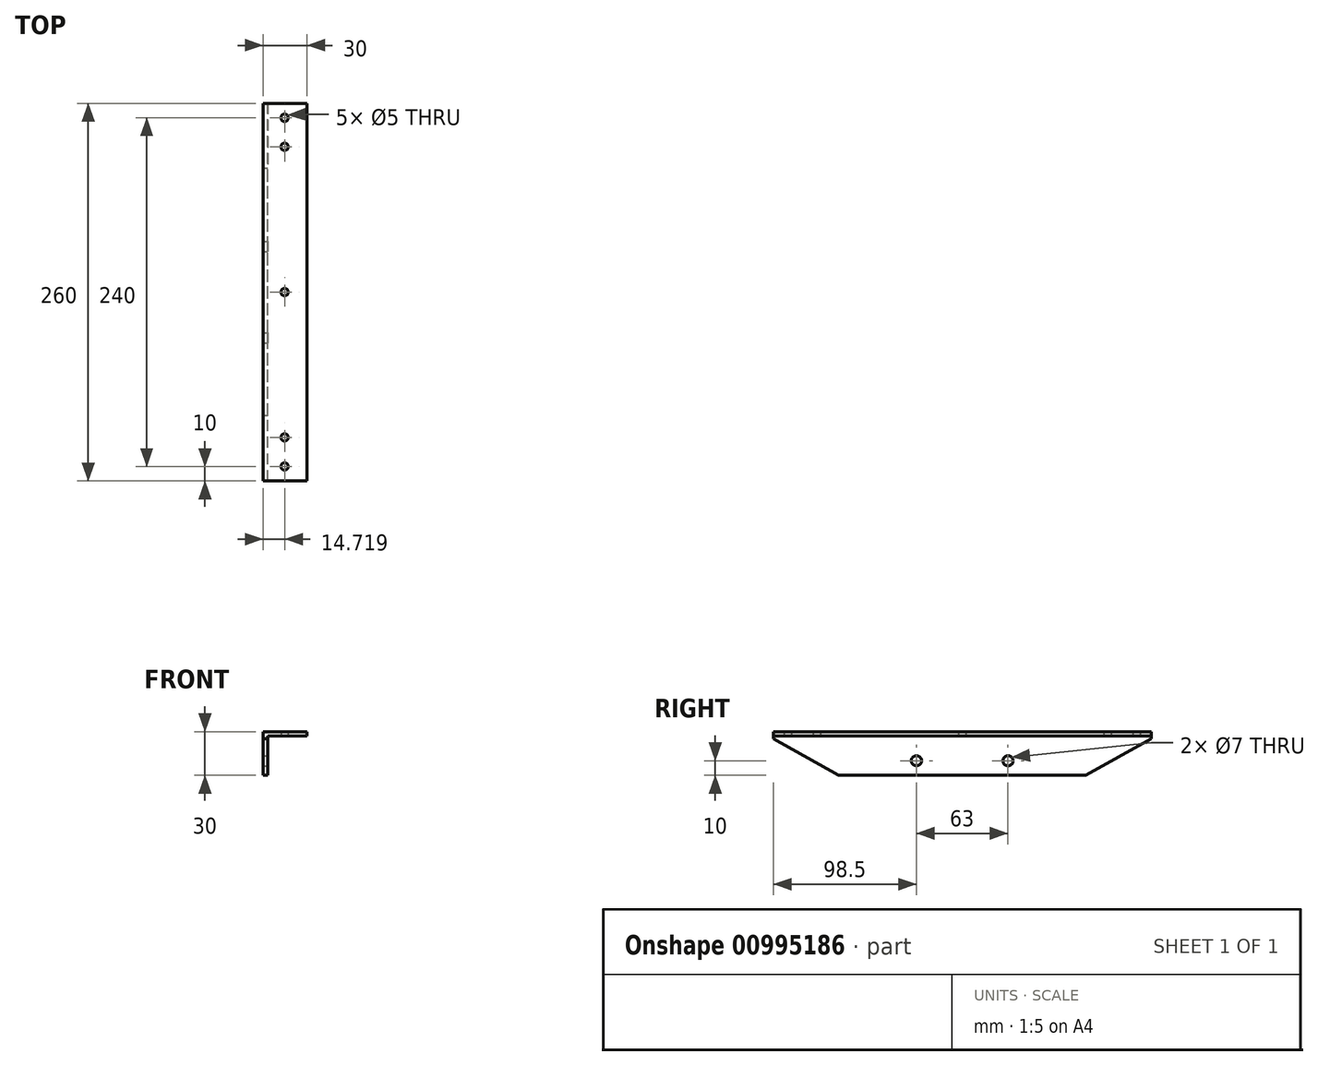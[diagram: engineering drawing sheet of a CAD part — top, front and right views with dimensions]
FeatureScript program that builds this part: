
annotation { "Feature Type Name" : "Feature", "Feature Type Description" : "" }
export const myFeature = defineFeature(function(context is Context, id is Id, definition is map)
    precondition{}
    {
        {
            var Q0;
            Q0=qCreatedBy(makeId("Front.planeOp"),FACE);
            var sketch = newSketch(context, id + "F0", { "sketchPlane" : qUnion([Q0])});
            skLineSegment(sketch, "E0", {"start": v(0, 0) * mm, "end": v(0, 30) * mm});
            skLineSegment(sketch, "E1", {"start": v(0, 30) * mm, "end": v(30, 30) * mm});
            skLineSegment(sketch, "E2", {"start": v(30, 30) * mm, "end": v(30, 27) * mm});
            skLineSegment(sketch, "E3", {"start": v(30, 27) * mm, "end": v(3, 27) * mm});
            skLineSegment(sketch, "E4", {"start": v(3, 27) * mm, "end": v(3, 0) * mm});
            skLineSegment(sketch, "E5", {"start": v(3, 0) * mm, "end": v(0, 0) * mm});
            skSolve(sketch);
        }
        {
            var Q0;
            Q0=makeQuery(id+"F0.imprint","IMPRINT",FACE,{"disambiguationData":[TD([[makeQuery(id+"F0.imprint","IMPRINT",EDGE,{"derivedFrom":sQuery(id+"F0.wireOp",EDGE,"E0")}),-1.0]])]});
            extrude(context, id + "F1", {"entities" : qUnion([Q0]), "depth" : 260 * mm, "offsetDistance" : 25 * mm, "symmetric" : true});
        }
        {
            var Q0;
            Q0=makeQuery(id+"F1.opExtrude","SWEPT_FACE",FACE,{"disambiguationData":[OSD([sQuery(id+"F0.wireOp",EDGE,"E0")])]});
            var sketch = newSketch(context, id + "F2", { "sketchPlane" : qUnion([Q0])});
            skLineSegment(sketch, "E6", {"start": v(0, 30) * mm, "end": v(0, 10) * mm});
            skLineSegment(sketch, "E7", {"start": v(0, 10) * mm, "end": v(-31.5, 10) * mm});
            skLineSegment(sketch, "E8", {"start": v(0, 10) * mm, "end": v(31.5, 10) * mm});
            skSolve(sketch);
        }
        {
            var Q0;
            Q0=sQuery(id+"F2.wireOp",VERTEX,"E7.end");
            var Q1;
            Q1=sQuery(id+"F2.wireOp",VERTEX,"E8.end");
            var Q2;
            Q2=makeQuery(id+"F1.opExtrude","SWEPT_BODY",BODY,{"disambiguationData":[OSD([sQuery(id+"F0.wireOp",EDGE,"E0"),sQuery(id+"F0.wireOp",EDGE,"E1"),sQuery(id+"F0.wireOp",EDGE,"E2"),sQuery(id+"F0.wireOp",EDGE,"E3"),sQuery(id+"F0.wireOp",EDGE,"E4"),sQuery(id+"F0.wireOp",EDGE,"E5")])]});
            hole(context, id + "F3", {"style" : HoleStyle.SIMPLE, "endStyle" : HoleEndStyle.THROUGH, "holeDiameter" : 7 * mm, "majorDiameter" : 5 * mm, "isTappedThrough" : true, "tappedDepth" : 12 * mm, "tapClearance" : 3, "locations" : qUnion([Q0, Q1]), "scope" : qUnion([Q2]), "startStyle" : HoleStartStyle.PART});
        }
        {
            var Q0;
            Q0=makeQuery(id+"F1.opExtrude","SWEPT_FACE",FACE,{"disambiguationData":[OSD([sQuery(id+"F0.wireOp",EDGE,"E1")])]});
            var sketch = newSketch(context, id + "F4", { "sketchPlane" : qUnion([Q0])});
            skLineSegment(sketch, "E9", {"start": v(0, 0) * mm, "end": v(14.72, 0) * mm});
            skLineSegment(sketch, "E10", {"start": v(14.72, 0) * mm, "end": v(14.72, 100) * mm});
            skLineSegment(sketch, "E11", {"start": v(14.72, 0) * mm, "end": v(14.72, -100) * mm});
            skLineSegment(sketch, "E12", {"start": v(14.72, -100) * mm, "end": v(14.72, -120) * mm});
            skLineSegment(sketch, "E13", {"start": v(14.72, 100) * mm, "end": v(14.72, 120) * mm});
            skSolve(sketch);
        }
        {
            var Q0;
            Q0=sQuery(id+"F4.wireOp",VERTEX,"1tQewzAj-UfQE-Z77g-f8Yq-8VD4JALRFgvb.end");
            var Q1;
            Q1=sQuery(id+"F4.wireOp",VERTEX,"1tQewzAj-UfQE-Z77g-f8Yq-8VD4JALRFgvb.start");
            var Q2;
            Q2=sQuery(id+"F4.wireOp",VERTEX,"LTQKht7b-NH9M-FIFn-inf1-8K7WugWQLx6k.start");
            var Q3;
            Q3=sQuery(id+"F4.wireOp",VERTEX,"E11.start");
            var Q4;
            Q4=sQuery(id+"F4.wireOp",VERTEX,"Bhl9sl7J-fMcb-BVDl-VWbh-HoV6IlCvf5ou.start");
            var Q5;
            Q5=sQuery(id+"F4.wireOp",VERTEX,"l9MGoOj7-PQq2-p4TO-Y7hb-mTCIAhJtyrPD.start");
            var Q6;
            Q6=sQuery(id+"F4.wireOp",VERTEX,"l9MGoOj7-PQq2-p4TO-Y7hb-mTCIAhJtyrPD.end");
            var Q7;
            Q7=sQuery(id+"F4.wireOp",VERTEX,"gbc2nK7E-ztz0-IBhr-DfQU-EQeF7ijxsCjM.end");
            var Q8;
            Q8=sQuery(id+"F4.wireOp",VERTEX,"ZtBBAAtL-lso0-mhiq-NLzV-Yrly4486QW8c.end");
            var Q9;
            Q9=sQuery(id+"F4.wireOp",VERTEX,"SlA1qLtV-EIWa-L179-yqE0-1lIOZillnqvx.end");
            var Q10;
            Q10=sQuery(id+"F4.wireOp",VERTEX,"J0ETeXer-Zvjq-F775-bQsg-4Zvr5mP6p7do.end");
            var Q11;
            Q11=sQuery(id+"F4.wireOp",VERTEX,"E11.end");
            var Q12;
            Q12=sQuery(id+"F4.wireOp",VERTEX,"E10.end");
            var Q13;
            Q13=sQuery(id+"F4.wireOp",VERTEX,"E12.end");
            var Q14;
            Q14=sQuery(id+"F4.wireOp",VERTEX,"E13.end");
            var Q15;
            Q15=makeQuery(id+"F1.opExtrude","SWEPT_BODY",BODY,{"disambiguationData":[OSD([sQuery(id+"F0.wireOp",EDGE,"E0"),sQuery(id+"F0.wireOp",EDGE,"E1"),sQuery(id+"F0.wireOp",EDGE,"E2"),sQuery(id+"F0.wireOp",EDGE,"E3"),sQuery(id+"F0.wireOp",EDGE,"E4"),sQuery(id+"F0.wireOp",EDGE,"E5")])]});
            hole(context, id + "F5", {"style" : HoleStyle.SIMPLE, "endStyle" : HoleEndStyle.THROUGH, "holeDiameter" : 5 * mm, "majorDiameter" : 5 * mm, "isTappedThrough" : true, "tappedDepth" : 12 * mm, "tapClearance" : 3, "locations" : qUnion([Q0, Q1, Q2, Q3, Q4, Q5, Q6, Q7, Q8, Q9, Q10, Q11, Q12, Q13, Q14]), "scope" : qUnion([Q15]), "startStyle" : HoleStartStyle.PART});
        }
        {
            var Q0;
            Q0=makeQuery(id+"F1.opExtrude","SWEPT_FACE",FACE,{"disambiguationData":[OSD([sQuery(id+"F0.wireOp",EDGE,"E0")])]});
            var sketch = newSketch(context, id + "F6", { "sketchPlane" : qUnion([Q0])});
            skLineSegment(sketch, "E14", {"start": v(-130, 25) * mm, "end": v(-130, 0) * mm});
            skLineSegment(sketch, "E15", {"start": v(-130, 0) * mm, "end": v(-85, 0) * mm});
            skLineSegment(sketch, "E16", {"start": v(-85, 0) * mm, "end": v(-130, 25) * mm});
            skLineSegment(sketch, "E17", {"start": v(130, 25) * mm, "end": v(130, 0) * mm});
            skLineSegment(sketch, "E18", {"start": v(130, 0) * mm, "end": v(85, 0) * mm});
            skLineSegment(sketch, "E19", {"start": v(85, 0) * mm, "end": v(130, 25) * mm});
            skSolve(sketch);
        }
        {
            var Q0;
            Q0=qSketchRegion(id+"F6",true);
            extrude(context, id + "F7", {"entities" : qUnion([Q0]), "operationType" : NewBodyOperationType.REMOVE, "oppositeDirection" : true, "depth" : 25 * mm, "offsetDistance" : 25 * mm});
        }
    });
